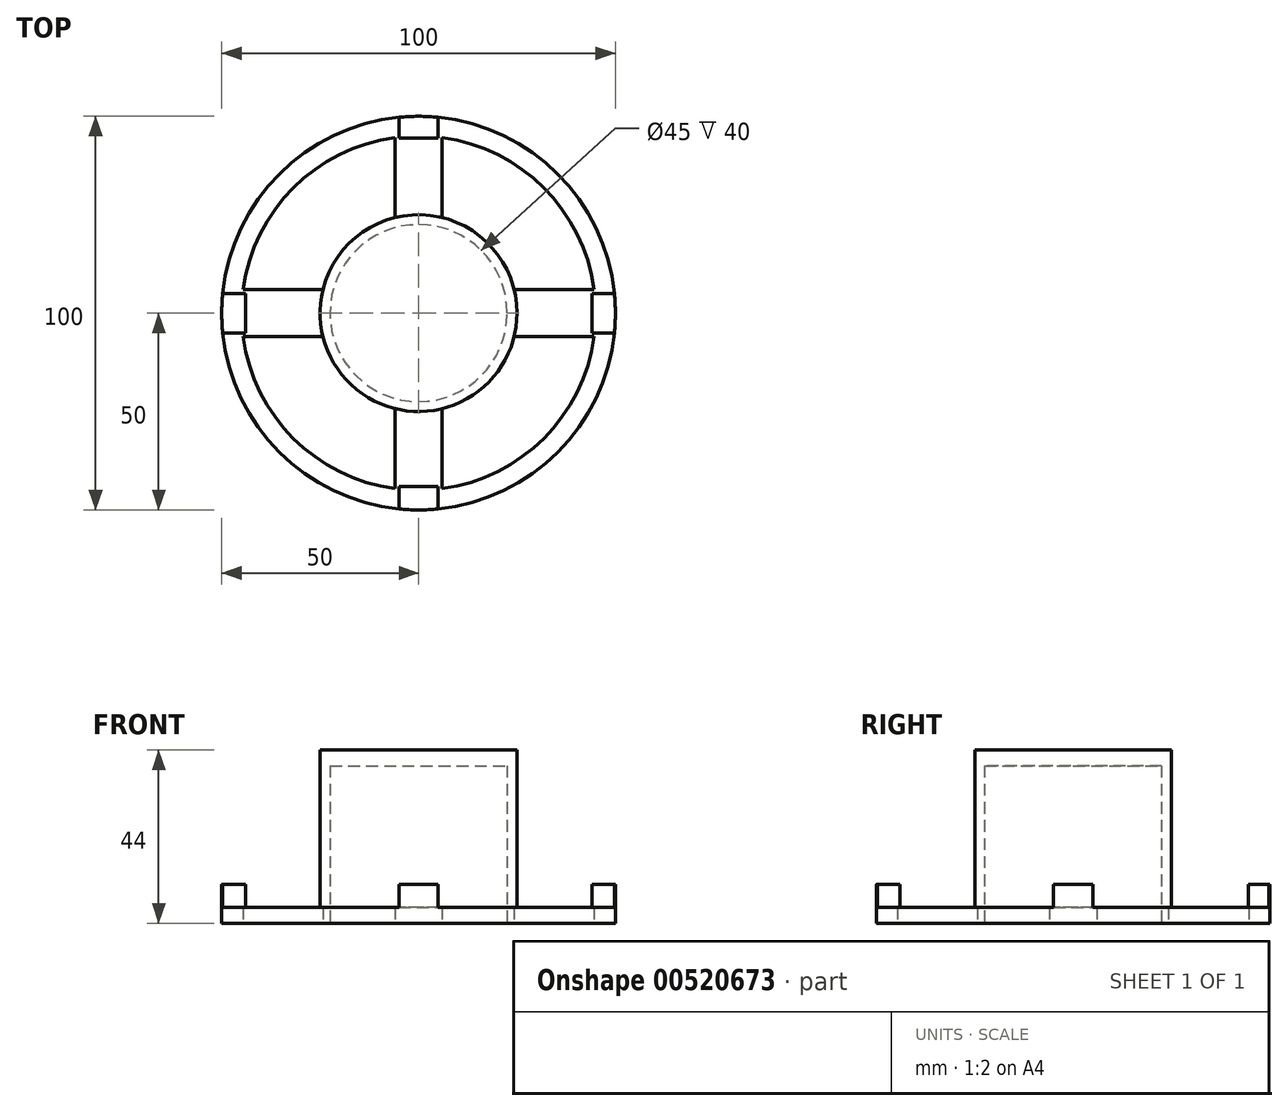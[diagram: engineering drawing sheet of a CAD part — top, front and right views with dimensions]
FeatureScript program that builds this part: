
annotation { "Feature Type Name" : "Feature", "Feature Type Description" : "" }
export const myFeature = defineFeature(function(context is Context, id is Id, definition is map)
    precondition{}
    {
        {
            var Q0;
            Q0=qCreatedBy(makeId("Top.planeOp"),FACE);
            var sketch = newSketch(context, id + "F0", { "sketchPlane" : qUnion([Q0])});
            skCircle(sketch, "E0", {"center": v(0, 0) * mm, "radius": 50 * mm});
            skSolve(sketch);
        }
        {
            var Q0;
            Q0=qSketchRegion(id+"F0",true);
            extrude(context, id + "F1", {"entities" : qUnion([Q0]), "depth" : 4 * mm, "offsetDistance" : 25 * mm});
        }
        {
            var Q0;
            Q0=makeQuery(id+"F1.opExtrude","CAP_FACE",FACE,{"disambiguationData":[OSD([sQuery(id+"F0.wireOp",EDGE,"E0")])],"isStart":false});
            var sketch = newSketch(context, id + "F2", { "sketchPlane" : qUnion([Q0])});
            skCircle(sketch, "E1", {"center": v(0, 0) * mm, "radius": 25 * mm});
            skSolve(sketch);
        }
        {
            var Q0;
            Q0=qSketchRegion(id+"F2",true);
            extrude(context, id + "F3", {"entities" : qUnion([Q0]), "operationType" : NewBodyOperationType.ADD, "depth" : 40 * mm, "offsetDistance" : 25 * mm});
        }
        {
            var Q0;
            Q0=makeQuery(id+"F1.opExtrude","CAP_FACE",FACE,{"disambiguationData":[OSD([sQuery(id+"F0.wireOp",EDGE,"E0")])],"isStart":false});
            var sketch = newSketch(context, id + "F4", { "sketchPlane" : qUnion([Q0])});
            skLineSegment(sketch, "E2.bottom", {"start": v(5, 50) * mm, "end": v(-5, 50) * mm});
            skLineSegment(sketch, "E2.top", {"start": v(5, 44.5) * mm, "end": v(-5, 44.5) * mm});
            skLineSegment(sketch, "E2.left", {"start": v(5, 50) * mm, "end": v(5, 44.5) * mm});
            skLineSegment(sketch, "E2.right", {"start": v(-5, 50) * mm, "end": v(-5, 44.5) * mm});
            skLineSegment(sketch, "E3.bottom", {"start": v(5, -44) * mm, "end": v(-5, -44) * mm});
            skLineSegment(sketch, "E3.top", {"start": v(5, -50) * mm, "end": v(-5, -50) * mm});
            skLineSegment(sketch, "E3.left", {"start": v(5, -44) * mm, "end": v(5, -50) * mm});
            skLineSegment(sketch, "E3.right", {"start": v(-5, -44) * mm, "end": v(-5, -50) * mm});
            skLineSegment(sketch, "E4.bottom", {"start": v(-44, 5) * mm, "end": v(-44, -5) * mm});
            skLineSegment(sketch, "E4.top", {"start": v(-50, 5) * mm, "end": v(-50, -5) * mm});
            skLineSegment(sketch, "E4.left", {"start": v(-50, 5) * mm, "end": v(-44, 5) * mm});
            skLineSegment(sketch, "E4.right", {"start": v(-50, -5) * mm, "end": v(-44, -5) * mm});
            skLineSegment(sketch, "E5.bottom", {"start": v(50, -5) * mm, "end": v(50, 5) * mm});
            skLineSegment(sketch, "E5.top", {"start": v(44, -5) * mm, "end": v(44, 5) * mm});
            skLineSegment(sketch, "E5.left", {"start": v(50, -5) * mm, "end": v(44, -5) * mm});
            skLineSegment(sketch, "E5.right", {"start": v(50, 5) * mm, "end": v(44, 5) * mm});
            skSolve(sketch);
        }
        {
            var Q0;
            {var subQ4=sQuery(id+"F4.wireOp",EDGE,"E2.top");Q0=makeQuery(id+"F4.imprint","IMPRINT",FACE,{"disambiguationData":[TD([[makeQuery(id+"F4.imprint","IMPRINT",EDGE,{"derivedFrom":subQ4}),-1.0]])]});}
            extrude(context, id + "F5", {"entities" : qUnion([Q0]), "operationType" : NewBodyOperationType.ADD, "depth" : 5.8 * mm, "offsetDistance" : 25 * mm});
        }
        {
            var Q0;
            {var subQ5=sQuery(id+"F4.wireOp",EDGE,"E3.bottom");Q0=makeQuery(id+"F4.imprint","IMPRINT",FACE,{"disambiguationData":[TD([[makeQuery(id+"F4.imprint","IMPRINT",EDGE,{"derivedFrom":subQ5}),1.0]])]});}
            extrude(context, id + "F6", {"entities" : qUnion([Q0]), "operationType" : NewBodyOperationType.ADD, "depth" : 5.8 * mm, "offsetDistance" : 25 * mm});
        }
        {
            var Q0;
            {var subQ5=sQuery(id+"F4.wireOp",EDGE,"E4.bottom");Q0=makeQuery(id+"F4.imprint","IMPRINT",FACE,{"disambiguationData":[TD([[makeQuery(id+"F4.imprint","IMPRINT",EDGE,{"derivedFrom":subQ5}),-1.0]])]});}
            var Q1;
            {var subQ1=sQuery(id+"F4.wireOp",EDGE,"E5.top");Q1=makeQuery(id+"F4.imprint","IMPRINT",FACE,{"disambiguationData":[TD([[makeQuery(id+"F4.imprint","IMPRINT",EDGE,{"derivedFrom":subQ1}),-1.0]])]});}
            extrude(context, id + "F7", {"entities" : qUnion([Q0, Q1]), "operationType" : NewBodyOperationType.ADD, "depth" : 5.8 * mm, "offsetDistance" : 25 * mm});
        }
        {
            var Q0;
            Q0=qCreatedBy(makeId("Top.planeOp"),FACE);
            var sketch = newSketch(context, id + "F8", { "sketchPlane" : qUnion([Q0])});
            skCircle(sketch, "E6", {"center": v(0, 0) * mm, "radius": 45 * mm});
            skSolve(sketch);
        }
        {
            var Q0;
            Q0 = qSketchRegion(id + "F8", true);
            extrude(context, id + "F9", {"entities" : qUnion([Q0]), "operationType" : NewBodyOperationType.REMOVE, "depth" : 4 * mm, "offsetDistance" : 25 * mm});
        }
        {
            var Q0;
            Q0=qCreatedBy(makeId("Top.planeOp"),FACE);
            var sketch = newSketch(context, id + "F10", { "sketchPlane" : qUnion([Q0])});
            skLineSegment(sketch, "E7.bottom", {"start": v(-6, 46.88) * mm, "end": v(6, 46.88) * mm});
            skLineSegment(sketch, "E7.top", {"start": v(-6, 0) * mm, "end": v(6, 0) * mm});
            skLineSegment(sketch, "E7.left", {"start": v(-6, 46.88) * mm, "end": v(-6, 0) * mm});
            skLineSegment(sketch, "E7.right", {"start": v(6, 46.88) * mm, "end": v(6, 0) * mm});
            skLineSegment(sketch, "E8.top", {"start": v(-6, -46.78) * mm, "end": v(6, -46.78) * mm});
            skLineSegment(sketch, "E8.left", {"start": v(-6, 0) * mm, "end": v(-6, -46.78) * mm});
            skLineSegment(sketch, "E8.right", {"start": v(6, 0) * mm, "end": v(6, -46.78) * mm});
            skLineSegment(sketch, "E9.bottom", {"start": v(0, -6) * mm, "end": v(46.83, -6) * mm});
            skLineSegment(sketch, "E9.top", {"start": v(0, 6) * mm, "end": v(46.83, 6) * mm});
            skLineSegment(sketch, "E9.left", {"start": v(0, -6) * mm, "end": v(0, 6) * mm});
            skLineSegment(sketch, "E9.right", {"start": v(46.83, -6) * mm, "end": v(46.83, 6) * mm});
            skLineSegment(sketch, "E10.bottom", {"start": v(0, 6) * mm, "end": v(-46.57, 6) * mm});
            skLineSegment(sketch, "E10.top", {"start": v(0, -6) * mm, "end": v(-46.57, -6) * mm});
            skLineSegment(sketch, "E10.left", {"start": v(0, 6) * mm, "end": v(0, -6) * mm});
            skLineSegment(sketch, "E10.right", {"start": v(-46.57, 6) * mm, "end": v(-46.57, -6) * mm});
            skSolve(sketch);
        }
        {
            var Q0;
            Q0 = qSketchRegion(id + "F10", true);
            extrude(context, id + "F11", {"entities" : qUnion([Q0]), "operationType" : NewBodyOperationType.ADD, "depth" : 4 * mm, "offsetDistance" : 25 * mm});
        }
        {
            var Q0;
            Q0=qCreatedBy(makeId("Top.planeOp"),FACE);
            var sketch = newSketch(context, id + "F12", { "sketchPlane" : qUnion([Q0])});
            skCircle(sketch, "E11", {"center": v(0, 0) * mm, "radius": 25 * mm});
            skSolve(sketch);
        }
        {
            var Q0;
            Q0 = qSketchRegion(id + "F12", true);
            extrude(context, id + "F13", {"entities" : qUnion([Q0]), "operationType" : NewBodyOperationType.ADD, "depth" : 5 * mm, "offsetDistance" : 25 * mm});
        }
        {
            var Q0;
            Q0=makeQuery(id+"F13.boolean.opBoolean","MERGE",FACE,{"derivedFrom":[makeQuery(id+"F11.boolean.opBoolean","MERGE",FACE,{"derivedFrom":[makeQuery(id+"F1.opExtrude","CAP_FACE",FACE,{"disambiguationData":[OSD([sQuery(id+"F0.wireOp",EDGE,"E0")])],"isStart":true}),makeQuery(id+"F11.opExtrude","CAP_FACE",FACE,{"disambiguationData":[OSD([sQuery(id+"F10.wireOp",EDGE,"E7.bottom"),sQuery(id+"F10.wireOp",EDGE,"E7.left"),sQuery(id+"F10.wireOp",EDGE,"E7.right"),sQuery(id+"F10.wireOp",EDGE,"E8.top"),sQuery(id+"F10.wireOp",EDGE,"E8.left"),sQuery(id+"F10.wireOp",EDGE,"E8.right"),sQuery(id+"F10.wireOp",EDGE,"E9.bottom"),sQuery(id+"F10.wireOp",EDGE,"E9.top"),sQuery(id+"F10.wireOp",EDGE,"E9.right"),sQuery(id+"F10.wireOp",EDGE,"E10.bottom"),sQuery(id+"F10.wireOp",EDGE,"E10.top"),sQuery(id+"F10.wireOp",EDGE,"E10.right")])],"isStart":true})]}),makeQuery(id+"F13.opExtrude","CAP_FACE",FACE,{"disambiguationData":[OSD([sQuery(id+"F12.wireOp",EDGE,"E11")])],"isStart":true})]});
            var sketch = newSketch(context, id + "F14", { "sketchPlane" : qUnion([Q0])});
            skCircle(sketch, "E12", {"center": v(0, 0) * mm, "radius": 22.5 * mm});
            skSolve(sketch);
        }
        {
            var Q0;
            Q0 = qSketchRegion(id + "F14", true);
            extrude(context, id + "F15", {"entities" : qUnion([Q0]), "operationType" : NewBodyOperationType.REMOVE, "oppositeDirection" : true, "depth" : 40 * mm, "offsetDistance" : 25 * mm});
        }
    });
